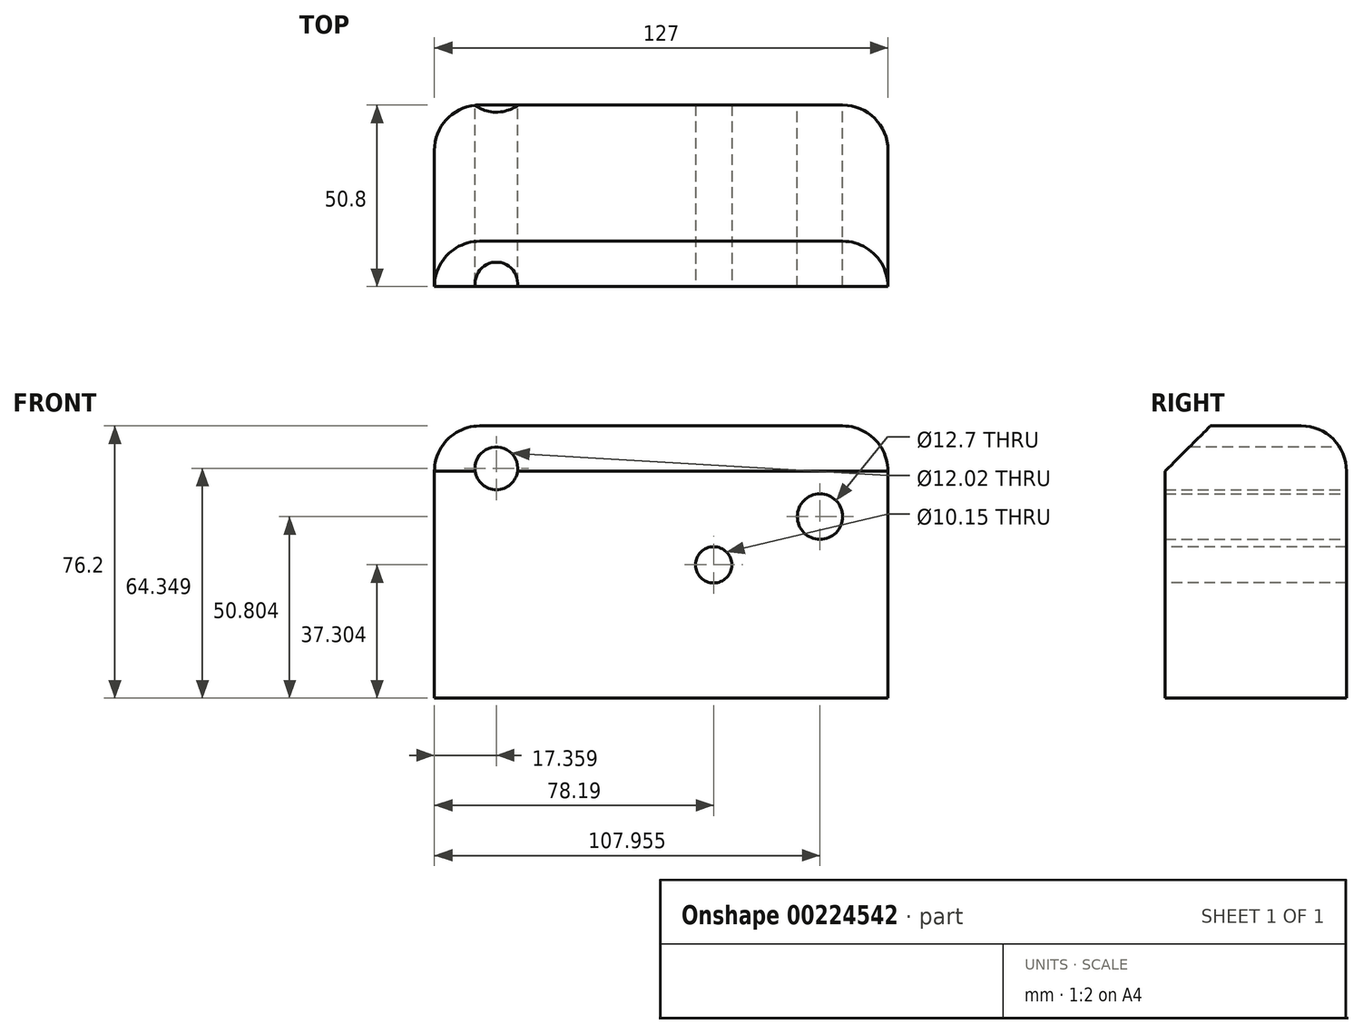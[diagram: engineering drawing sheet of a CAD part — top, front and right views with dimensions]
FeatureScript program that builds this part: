
annotation { "Feature Type Name" : "Feature", "Feature Type Description" : "" }
export const myFeature = defineFeature(function(context is Context, id is Id, definition is map)
    precondition{}
    {
        {
            var Q0;
            Q0=qCreatedBy(makeId("Front.planeOp"),FACE);
            var sketch = newSketch(context, id + "F0", { "sketchPlane" : qUnion([Q0])});
            skLineSegment(sketch, "E0.bottom", {"start": v(-78.19, 85.4) * mm, "end": v(48.81, 85.4) * mm});
            skLineSegment(sketch, "E0.top", {"start": v(-78.19, 9.2) * mm, "end": v(48.81, 9.2) * mm});
            skLineSegment(sketch, "E0.left", {"start": v(-78.19, 85.4) * mm, "end": v(-78.19, 9.2) * mm});
            skLineSegment(sketch, "E0.right", {"start": v(48.81, 85.4) * mm, "end": v(48.81, 9.2) * mm});
            skCircle(sketch, "E1", {"center": v(29.76, 60) * mm, "radius": 6.35 * mm});
            skCircle(sketch, "E2", {"center": v(-60.83, 73.55) * mm, "radius": 6 * mm});
            skSolve(sketch);
        }
        {
            var Q0;
            Q0=makeQuery(id+"F0.imprint","IMPRINT",FACE,{"disambiguationData":[TD([[makeQuery(id+"F0.imprint","IMPRINT",EDGE,{"derivedFrom":sQuery(id+"F0.wireOp",EDGE,"E0.bottom")}),-1.0]])]});
            extrude(context, id + "F1", {"entities" : qUnion([Q0]), "depth" : 50.8 * mm});
        }
        {
            var Q0;
            Q0=makeQuery(id+"F1.opExtrude","CAP_FACE",FACE,{"disambiguationData":[OSD([sQuery(id+"F0.wireOp",EDGE,"E0.bottom"),sQuery(id+"F0.wireOp",EDGE,"E0.top"),sQuery(id+"F0.wireOp",EDGE,"E0.left"),sQuery(id+"F0.wireOp",EDGE,"E0.right"),sQuery(id+"F0.wireOp",EDGE,"E1"),sQuery(id+"F0.wireOp",EDGE,"E2")])],"isStart":false});
            var sketch = newSketch(context, id + "F2", { "sketchPlane" : qUnion([Q0])});
            skCircle(sketch, "E3", {"center": v(0, 46.5) * mm, "radius": 5.07 * mm});
            skSolve(sketch);
        }
        {
            var Q0;
            Q0=makeQuery(id+"F2.imprint","IMPRINT",FACE,{"disambiguationData":[TD([[makeQuery(id+"F2.imprint","IMPRINT",EDGE,{"derivedFrom":sQuery(id+"F2.wireOp",EDGE,"E3")}),1.0]])]});
            extrude(context, id + "F3", {"entities" : qUnion([Q0]), "operationType" : NewBodyOperationType.REMOVE, "oppositeDirection" : true, "depth" : 72.14 * mm});
        }
        {
            var Q0;
            Q0=makeQuery(id+"F1.opExtrude","CAP_EDGE",EDGE,{"disambiguationData":[OSD([sQuery(id+"F0.wireOp",EDGE,"E0.bottom")])],"isStart":false});
            chamfer(context, id + "F4", {"entities" : qUnion([Q0]), "width" : 12.7 * mm, "tangentPropagation" : true});
        }
        {
            var Q0;
            Q0=makeQuery(id+"F1.opExtrude","CAP_EDGE",EDGE,{"disambiguationData":[OSD([sQuery(id+"F0.wireOp",EDGE,"E0.bottom")])],"isStart":true});
            fillet(context, id + "F5", {"entities" : qUnion([Q0]), "radius" : 12.7 * mm, "tangentPropagation" : true, "allowEdgeOverflow" : false});
        }
        {
            var Q0;
            Q0=makeQuery(id+"F1.opExtrude","SWEPT_EDGE",EDGE,{"disambiguationData":[OSD([sQuery(id+"F0.wireOp",EDGE,"E0.bottom"),sQuery(id+"F0.wireOp",EDGE,"E0.left")])]});
            var Q1;
            Q1=makeQuery(id+"F1.opExtrude","SWEPT_EDGE",EDGE,{"disambiguationData":[OSD([sQuery(id+"F0.wireOp",EDGE,"E0.bottom"),sQuery(id+"F0.wireOp",EDGE,"E0.right")])]});
            fillet(context, id + "F6", {"entities" : qUnion([Q0, Q1]), "radius" : 12.7 * mm, "tangentPropagation" : true, "allowEdgeOverflow" : false});
        }
    });
